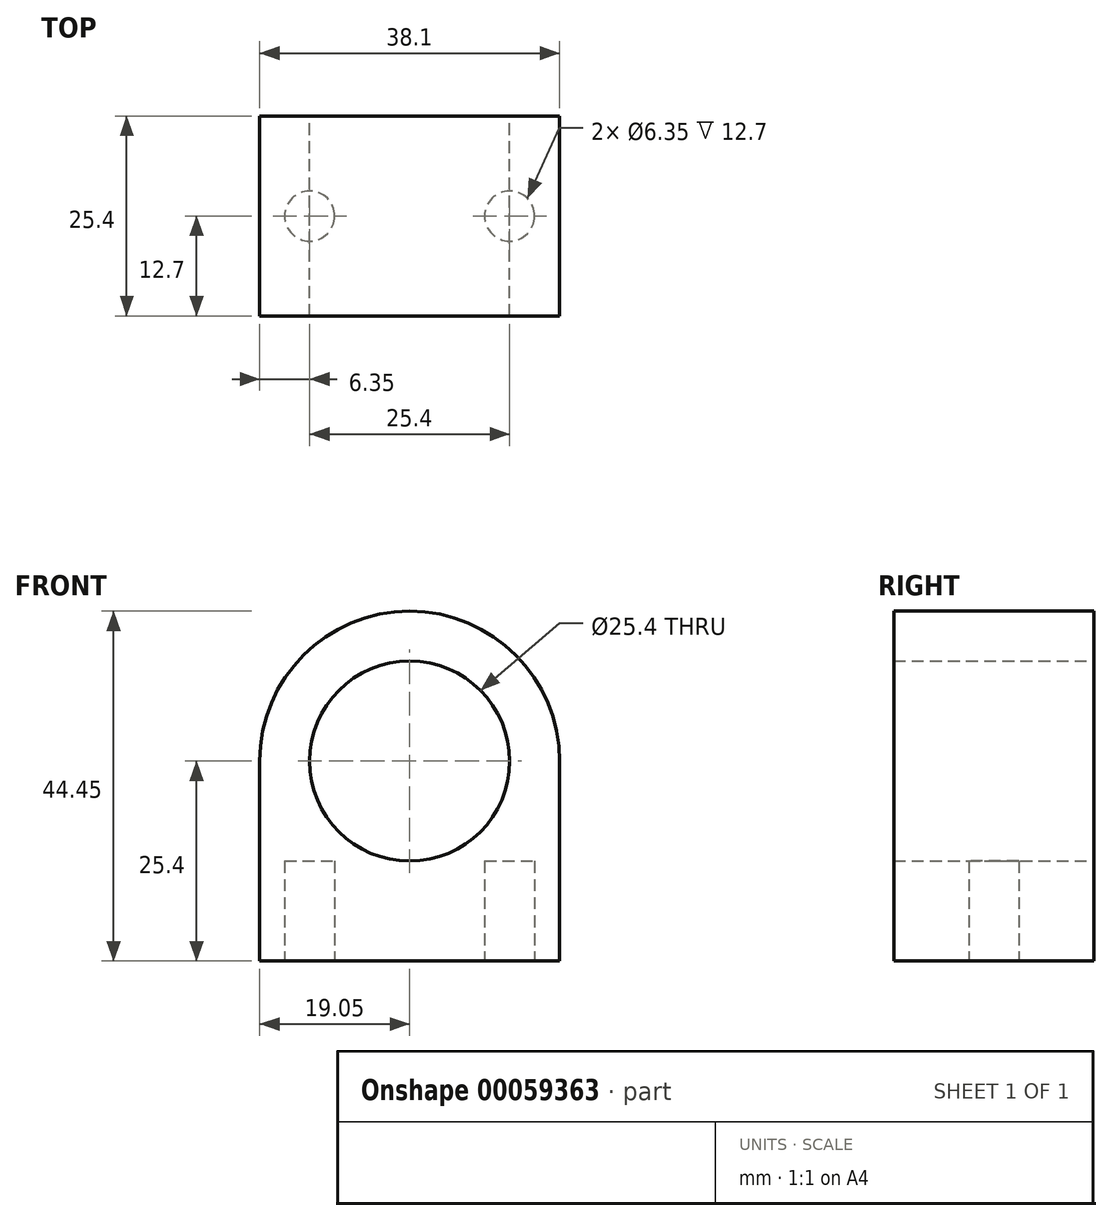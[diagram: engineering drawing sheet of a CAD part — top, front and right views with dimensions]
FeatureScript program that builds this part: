
annotation { "Feature Type Name" : "Feature", "Feature Type Description" : "" }
export const myFeature = defineFeature(function(context is Context, id is Id, definition is map)
    precondition{}
    {
        {
            var Q0;
            Q0=qCreatedBy(makeId("Front.planeOp"),FACE);
            var sketch = newSketch(context, id + "F0", { "sketchPlane" : qUnion([Q0])});
            skLineSegment(sketch, "E0", {"start": v(-100.63, 0) * mm, "end": v(95.74, 0) * mm, "construction": true});
            skLineSegment(sketch, "E1", {"start": v(0, 105.7) * mm, "end": v(0, -86.48) * mm, "construction": true});
            skCircle(sketch, "E2", {"center": v(0, 25.4) * mm, "radius": 12.7 * mm});
            skArc(sketch, "E3", {"start": v(19.05, 25.4) * mm, "mid": v(0, 44.45) * mm, "end": v(-19.05, 25.4) * mm});
            skLineSegment(sketch, "E4", {"start": v(-19.05, 25.4) * mm, "end": v(-19.05, 0) * mm});
            skLineSegment(sketch, "E5", {"start": v(19.05, 25.4) * mm, "end": v(19.05, 0) * mm});
            skLineSegment(sketch, "E6", {"start": v(19.05, 0) * mm, "end": v(-19.05, 0) * mm});
            skSolve(sketch);
        }
        {
            var Q0;
            Q0 = qSketchRegion(id + "F0", true);
            extrude(context, id + "F1", {"entities" : qUnion([Q0]), "endBound" : BoundingType.SYMMETRIC, "depth" : 25.4 * mm});
        }
        {
            var Q0;
            Q0=makeQuery(id+"F1.opExtrude","SWEPT_FACE",FACE,{"disambiguationData":[OSD([sQuery(id+"F0.wireOp",EDGE,"E6")])]});
            var sketch = newSketch(context, id + "F2", { "sketchPlane" : qUnion([Q0])});
            skLineSegment(sketch, "E7", {"start": v(-40.05, 0) * mm, "end": v(38.26, 0) * mm, "construction": true});
            skLineSegment(sketch, "E8", {"start": v(0, 41.76) * mm, "end": v(0, -39.8) * mm, "construction": true});
            skLineSegment(sketch, "E9", {"start": v(-12.7, 18.32) * mm, "end": v(-12.7, -25.64) * mm, "construction": true});
            skLineSegment(sketch, "E10", {"start": v(12.7, 18.32) * mm, "end": v(12.7, -25.64) * mm, "construction": true});
            skCircle(sketch, "E11", {"center": v(-12.7, 0) * mm, "radius": 3.18 * mm});
            skCircle(sketch, "E12", {"center": v(12.7, 0) * mm, "radius": 3.18 * mm});
            skSolve(sketch);
        }
        {
            var Q0;
            Q0 = qSketchRegion(id + "F2", true);
            extrude(context, id + "F3", {"entities" : qUnion([Q0]), "operationType" : NewBodyOperationType.REMOVE, "oppositeDirection" : true, "depth" : 12.7 * mm});
        }
    });
